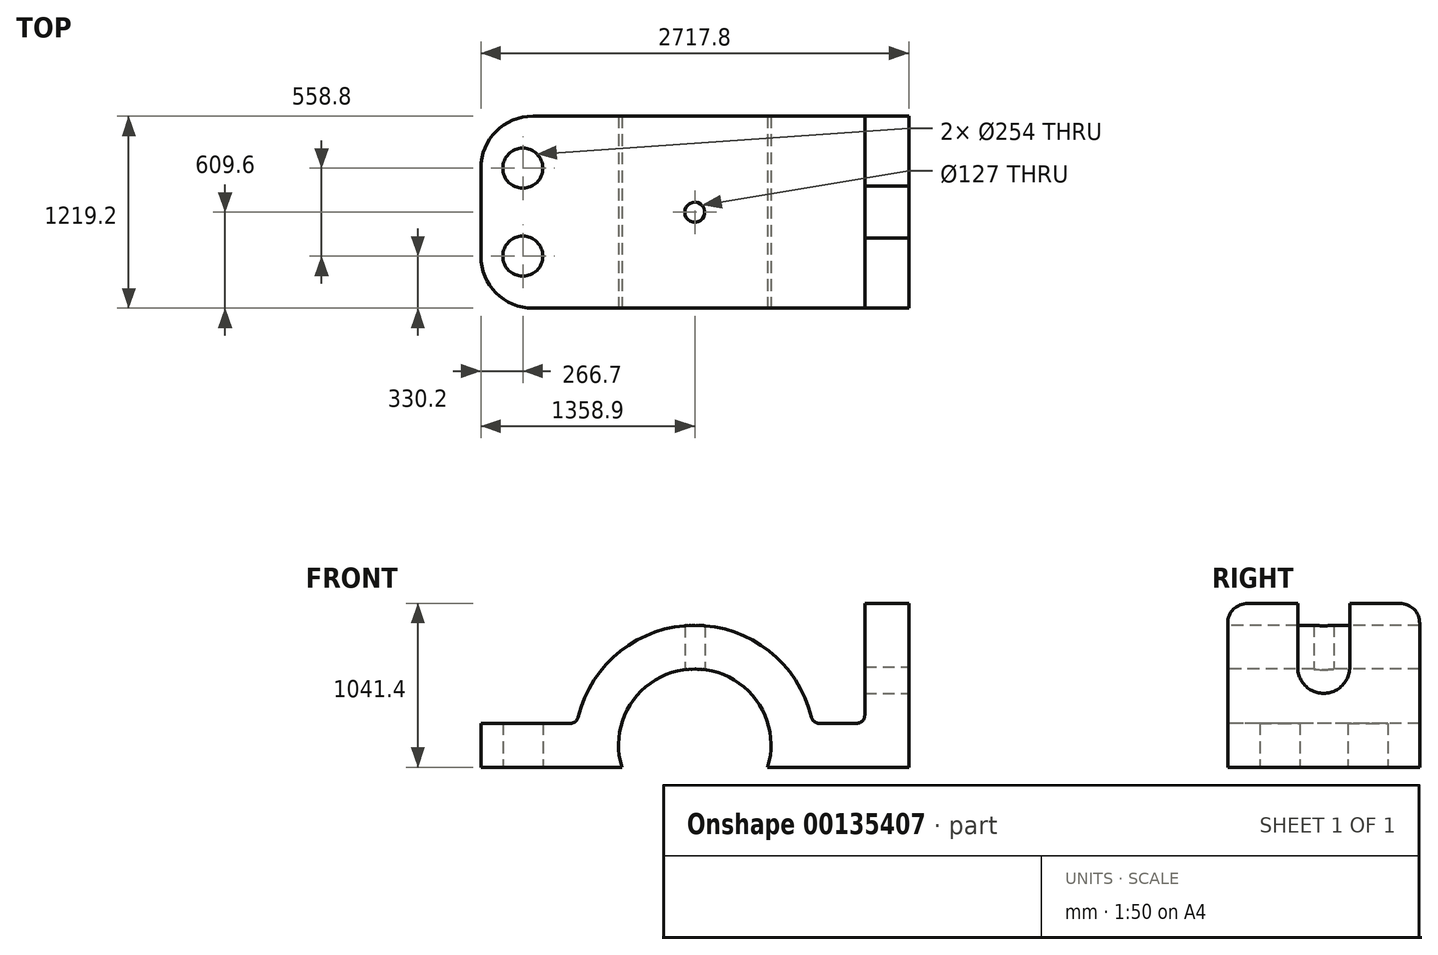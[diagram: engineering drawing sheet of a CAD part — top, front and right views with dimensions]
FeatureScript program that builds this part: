
annotation { "Feature Type Name" : "Feature", "Feature Type Description" : "" }
export const myFeature = defineFeature(function(context is Context, id is Id, definition is map)
    precondition{}
    {
        {
            var Q0;
            Q0=qCreatedBy(makeId("Front.planeOp"),FACE);
            var sketch = newSketch(context, id + "F0", { "sketchPlane" : qUnion([Q0])});
            skLineSegment(sketch, "E0.bottom", {"start": v(1028.7, 139.7) * mm, "end": v(790.16, 139.7) * mm});
            skLineSegment(sketch, "E0.top", {"start": v(1358.9, -139.7) * mm, "end": v(463.26, -139.7) * mm});
            skLineSegment(sketch, "E0.right", {"start": v(-1358.9, 139.7) * mm, "end": v(-1358.9, -139.7) * mm});
            skPoint(sketch, "E0.middle", {"position": v(0, 0) * mm});
            skArc(sketch, "E1", {"start": v(463.26, -139.7) * mm, "mid": v(0, 483.87) * mm, "end": v(-463.26, -139.7) * mm});
            skArc(sketch, "E2", {"start": v(740.78, 178.6) * mm, "mid": v(0, 762) * mm, "end": v(-740.78, 178.6) * mm});
            skLineSegment(sketch, "E3.trimOffspring", {"start": v(-463.26, -139.7) * mm, "end": v(-1358.9, -139.7) * mm});
            skLineSegment(sketch, "E4.trimOffspring", {"start": v(-790.16, 139.7) * mm, "end": v(-1358.9, 139.7) * mm});
            skLineSegment(sketch, "E5", {"start": v(1358.9, -139.7) * mm, "end": v(1358.9, 901.7) * mm});
            skLineSegment(sketch, "E6", {"start": v(1358.9, 901.7) * mm, "end": v(1079.5, 901.7) * mm});
            skLineSegment(sketch, "E7", {"start": v(1079.5, 901.7) * mm, "end": v(1079.5, 190.5) * mm});
            skPoint(sketch, "E8.orphan", {"position": v(1358.9, 139.7) * mm});
            skPoint(sketch, "E9.visualSharp", {"position": v(1079.5, 139.7) * mm});
            skArc(sketch, "E9.filletArc", {"start": v(1028.7, 139.7) * mm, "mid": v(1064.62, 154.58) * mm, "end": v(1079.5, 190.5) * mm});
            skPoint(sketch, "E10.visualSharp", {"position": v(749.08, 139.7) * mm});
            skArc(sketch, "E10.filletArc", {"start": v(740.78, 178.6) * mm, "mid": v(758.73, 150.6) * mm, "end": v(790.16, 139.7) * mm});
            skPoint(sketch, "E11.visualSharp", {"position": v(-749.08, 139.7) * mm});
            skArc(sketch, "E11.filletArc", {"start": v(-790.16, 139.7) * mm, "mid": v(-758.73, 150.6) * mm, "end": v(-740.78, 178.6) * mm});
            skSolve(sketch);
        }
        {
            var Q0;
            Q0 = qSketchRegion(id + "F0", true);
            extrude(context, id + "F1", {"entities" : qUnion([Q0]), "endBound" : BoundingType.SYMMETRIC, "oppositeDirection" : true, "depth" : 1219.2 * mm});
        }
        {
            var Q0;
            Q0=qCreatedBy(makeId("Top.planeOp"),FACE);
            var sketch = newSketch(context, id + "F2", { "sketchPlane" : qUnion([Q0])});
            skCircle(sketch, "E12", {"center": v(0, 0) * mm, "radius": 63.5 * mm});
            skLineSegment(sketch, "E13", {"start": v(0, 0) * mm, "end": v(-1092.2, 0) * mm, "construction": true});
            skLineSegment(sketch, "E14", {"start": v(-1092.2, 0) * mm, "end": v(-1092.2, 279.4) * mm, "construction": true});
            skCircle(sketch, "E15", {"center": v(-1092.2, 279.4) * mm, "radius": 127 * mm});
            skCircle(sketch, "E16.MirrorC", {"center": v(-1092.2, -279.4) * mm, "radius": 127 * mm});
            skSolve(sketch);
        }
        {
            var Q0;
            Q0 = qSketchRegion(id + "F2", true);
            extrude(context, id + "F3", {"entities" : qUnion([Q0]), "operationType" : NewBodyOperationType.REMOVE, "endBound" : BoundingType.THROUGH_ALL, "depth" : 25.4 * mm, "hasSecondDirection" : true, "secondDirectionBound" : SecondDirectionBoundingType.THROUGH_ALL, "secondDirectionOppositeDirection" : true, "secondDirectionDepth" : 25.4 * mm});
        }
        {
            var Q0;
            Q0=makeQuery(id+"F1.opExtrude","SWEPT_FACE",FACE,{"disambiguationData":[OSD([sQuery(id+"F0.wireOp",EDGE,"E5")])]});
            var sketch = newSketch(context, id + "F4", { "sketchPlane" : qUnion([Q0])});
            skLineSegment(sketch, "E17", {"start": v(0, -139.7) * mm, "end": v(0, 495.3) * mm, "construction": true});
            skPoint(sketch, "E17.endSnap0", {"position": v(0, -139.7) * mm});
            skArc(sketch, "E18", {"start": v(-165.05, 499.38) * mm, "mid": v(0, 330.2) * mm, "end": v(165.05, 499.38) * mm});
            skLineSegment(sketch, "E19", {"start": v(-165.05, 491.22) * mm, "end": v(-165.05, 901.7) * mm});
            skLineSegment(sketch, "E20.MirrorCS", {"start": v(165.05, 491.22) * mm, "end": v(165.05, 901.7) * mm});
            skLineSegment(sketch, "E21", {"start": v(-165.05, 901.7) * mm, "end": v(165.05, 901.7) * mm});
            skSolve(sketch);
        }
        {
            var Q0;
            Q0 = qSketchRegion(id + "F4", true);
            var Q1;
            Q1=makeQuery(id+"F1.opExtrude","SWEPT_FACE",FACE,{"disambiguationData":[OSD([sQuery(id+"F0.wireOp",EDGE,"E7")])]});
            extrude(context, id + "F5", {"entities" : qUnion([Q0]), "operationType" : NewBodyOperationType.REMOVE, "endBound" : BoundingType.UP_TO_SURFACE, "oppositeDirection" : true, "endBoundEntityFace" : qUnion([Q1]), "depth" : 25.4 * mm});
        }
        {
            var Q0;
            Q0=makeQuery(id+"F1.opExtrude","CAP_EDGE",EDGE,{"disambiguationData":[OSD([sQuery(id+"F0.wireOp",EDGE,"E6")])],"isStart":true});
            var Q1;
            Q1=makeQuery(id+"F1.opExtrude","CAP_EDGE",EDGE,{"disambiguationData":[OSD([sQuery(id+"F0.wireOp",EDGE,"E6")])],"isStart":false});
            fillet(context, id + "F6", {"entities" : qUnion([Q0, Q1]), "radius" : 127 * mm, "tangentPropagation" : true, "allowEdgeOverflow" : false});
        }
        {
            var Q0;
            Q0=makeQuery(id+"F1.opExtrude","CAP_EDGE",EDGE,{"disambiguationData":[OSD([sQuery(id+"F0.wireOp",EDGE,"E0.right")])],"isStart":true});
            var Q1;
            Q1=makeQuery(id+"F1.opExtrude","CAP_EDGE",EDGE,{"disambiguationData":[OSD([sQuery(id+"F0.wireOp",EDGE,"E0.right")])],"isStart":false});
            fillet(context, id + "F7", {"entities" : qUnion([Q0, Q1]), "radius" : 330.2 * mm, "tangentPropagation" : true, "allowEdgeOverflow" : false});
        }
    });
